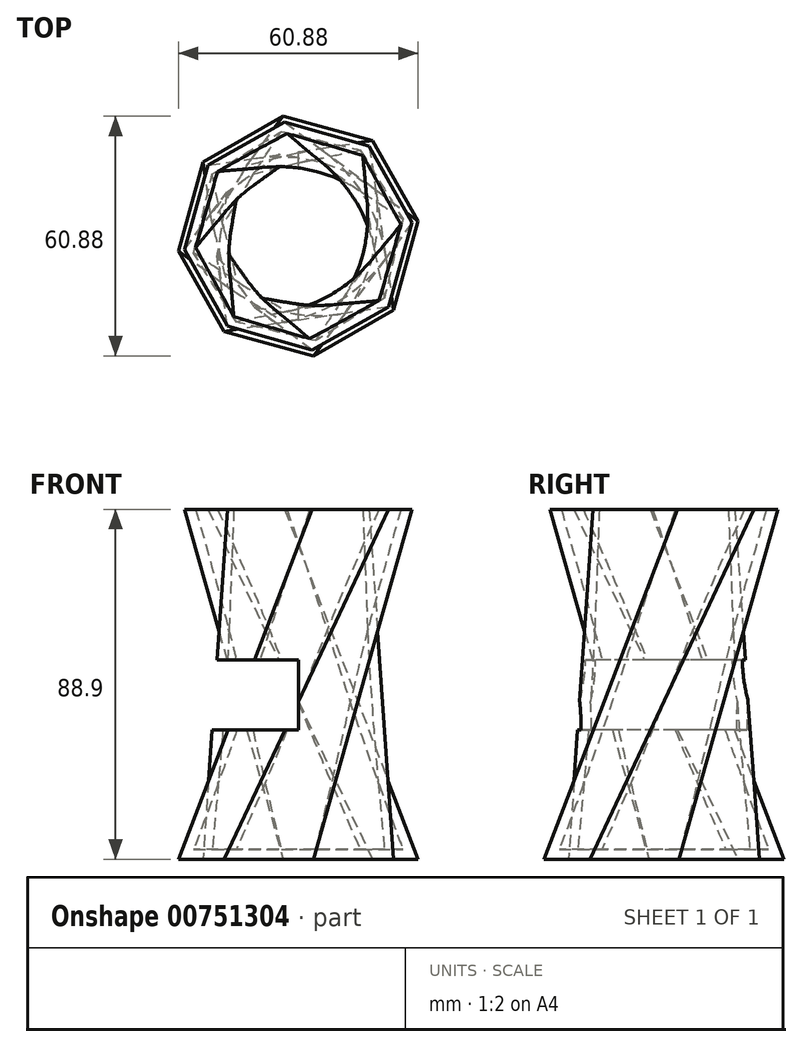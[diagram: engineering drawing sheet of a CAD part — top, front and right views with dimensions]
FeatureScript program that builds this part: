
annotation { "Feature Type Name" : "Feature", "Feature Type Description" : "" }
export const myFeature = defineFeature(function(context is Context, id is Id, definition is map)
    precondition{}
    {
        {
            var Q0;
            Q0=qCreatedBy(makeId("Top.planeOp"),FACE);
            var sketch = newSketch(context, id + "F0", { "sketchPlane" : qUnion([Q0])});
            skCircle(sketch, "E0.cCircle", {"center": v(0, 0) * mm, "radius": 28.34 * mm, "construction": true});
            skLineSegment(sketch, "E0.0", {"start": v(-24.23, 18.82) * mm, "end": v(-3.82, 30.44) * mm});
            skLineSegment(sketch, "E0.1", {"start": v(-3.82, 30.44) * mm, "end": v(18.82, 24.23) * mm});
            skLineSegment(sketch, "E0.2", {"start": v(18.82, 24.23) * mm, "end": v(30.44, 3.82) * mm});
            skLineSegment(sketch, "E0.3", {"start": v(30.44, 3.82) * mm, "end": v(24.23, -18.82) * mm});
            skLineSegment(sketch, "E0.4", {"start": v(24.23, -18.82) * mm, "end": v(3.82, -30.44) * mm});
            skLineSegment(sketch, "E0.5", {"start": v(3.82, -30.44) * mm, "end": v(-18.82, -24.23) * mm});
            skLineSegment(sketch, "E0.6", {"start": v(-18.82, -24.23) * mm, "end": v(-30.44, -3.82) * mm});
            skLineSegment(sketch, "E0.7", {"start": v(-30.44, -3.82) * mm, "end": v(-24.23, 18.82) * mm});
            skPoint(sketch, "E0.0.midPoint", {"position": v(-14.02, 24.63) * mm});
            skSolve(sketch);
        }
        {
            var Q0;
            Q0=makeQuery(id+"F0.imprint","IMPRINT",FACE,{"disambiguationData":[TD([[makeQuery(id+"F0.imprint","IMPRINT",EDGE,{"derivedFrom":sQuery(id+"F0.wireOp",EDGE,"E0.0")}),-1.0]])]});
            cPlane(context, id + "F1", {"entities" : qUnion([Q0]), "cplaneType" : CPlaneType.OFFSET, "offset" : 88.9 * mm, "width" : 152.4 * mm, "height" : 152.4 * mm});
        }
        {
            var Q0;
            Q0=qCreatedBy(id+"F1.planeOp",FACE);
            var sketch = newSketch(context, id + "F2", { "sketchPlane" : qUnion([Q0])});
            skCircle(sketch, "E1.cCircle", {"center": v(0, 0) * mm, "radius": 26.91 * mm, "construction": true});
            skLineSegment(sketch, "E1.0", {"start": v(-22.9, 18) * mm, "end": v(-3.47, 28.92) * mm});
            skLineSegment(sketch, "E1.1", {"start": v(-3.47, 28.92) * mm, "end": v(18, 22.9) * mm});
            skLineSegment(sketch, "E1.2", {"start": v(18, 22.9) * mm, "end": v(28.92, 3.47) * mm});
            skLineSegment(sketch, "E1.3", {"start": v(28.92, 3.47) * mm, "end": v(22.9, -18) * mm});
            skLineSegment(sketch, "E1.4", {"start": v(22.9, -18) * mm, "end": v(3.47, -28.92) * mm});
            skLineSegment(sketch, "E1.5", {"start": v(3.47, -28.92) * mm, "end": v(-18, -22.9) * mm});
            skLineSegment(sketch, "E1.6", {"start": v(-18, -22.9) * mm, "end": v(-28.92, -3.47) * mm});
            skLineSegment(sketch, "E1.7", {"start": v(-28.92, -3.47) * mm, "end": v(-22.9, 18) * mm});
            skPoint(sketch, "E1.0.midPoint", {"position": v(-13.19, 23.46) * mm});
            skSolve(sketch);
        }
        {
            var Q0;
            Q0=makeQuery(id+"F2.imprint","IMPRINT",FACE,{"disambiguationData":[TD([[makeQuery(id+"F2.imprint","IMPRINT",EDGE,{"derivedFrom":sQuery(id+"F2.wireOp",EDGE,"E1.0")}),-1.0]])]});
            var Q1;
            Q1=makeQuery(id+"F0.imprint","IMPRINT",FACE,{"disambiguationData":[TD([[makeQuery(id+"F0.imprint","IMPRINT",EDGE,{"derivedFrom":sQuery(id+"F0.wireOp",EDGE,"E0.0")}),-1.0]])]});
            var Q2;
            Q2=sQuery(id+"F2.wireOp",VERTEX,"E1.7.start");
            var Q3;
            Q3=sQuery(id+"F0.wireOp",VERTEX,"E0.1.start");
            loft(context, id + "F3", {"sheetProfilesArray" : [{ "sheetProfileEntities" : qUnion([Q0]) }, { "sheetProfileEntities" : qUnion([Q1]) }], "matchConnections" : true, "connections" : [{ "connectionEntities" : qUnion([Q2, Q3]), "connectionEdgeQueries" : qUnion([]), "connectionEdgeParameters" : [] }]});
        }
        {
            var Q0;
            Q0=makeQuery(id+"F3.opLoft","CAP_FACE",FACE,{"disambiguationData":[OSD([makeQuery(id+"F2.imprint","IMPRINT",FACE,{"disambiguationData":[TD([[makeQuery(id+"F2.imprint","IMPRINT",EDGE,{"derivedFrom":sQuery(id+"F2.wireOp",EDGE,"E1.0")}),-1.0]])]})])],"isStart":true});
            shell(context, id + "F4", {"entities" : qUnion([Q0]), "thickness" : 2.54 * mm});
        }
        {
            var Q0;
            Q0=qCreatedBy(makeId("Right.planeOp"),FACE);
            var sketch = newSketch(context, id + "F5", { "sketchPlane" : qUnion([Q0])});
            skLineSegment(sketch, "E2.bottom", {"start": v(50.14, 207.02) * mm, "end": v(32.62, 207.02) * mm});
            skLineSegment(sketch, "E2.top", {"start": v(50.14, 207.74) * mm, "end": v(32.62, 207.74) * mm});
            skLineSegment(sketch, "E2.left", {"start": v(50.14, 207.02) * mm, "end": v(50.14, 207.74) * mm});
            skLineSegment(sketch, "E2.right", {"start": v(32.62, 207.02) * mm, "end": v(32.62, 207.74) * mm});
            skLineSegment(sketch, "E3.bottom", {"start": v(-38.76, 50.64) * mm, "end": v(50.14, 50.64) * mm});
            skLineSegment(sketch, "E3.top", {"start": v(-38.76, 32.86) * mm, "end": v(50.14, 32.86) * mm});
            skLineSegment(sketch, "E3.left", {"start": v(-38.76, 50.64) * mm, "end": v(-38.76, 32.86) * mm});
            skLineSegment(sketch, "E3.right", {"start": v(50.14, 50.64) * mm, "end": v(50.14, 32.86) * mm});
            skSolve(sketch);
        }
        {
            var Q0;
            Q0=qSketchRegion(id+"F5",true);
            extrude(context, id + "F6", {"entities" : qUnion([Q0]), "operationType" : NewBodyOperationType.REMOVE, "oppositeDirection" : true, "depth" : 25.4 * mm, "offsetDistance" : 25.4 * mm});
        }
    });
